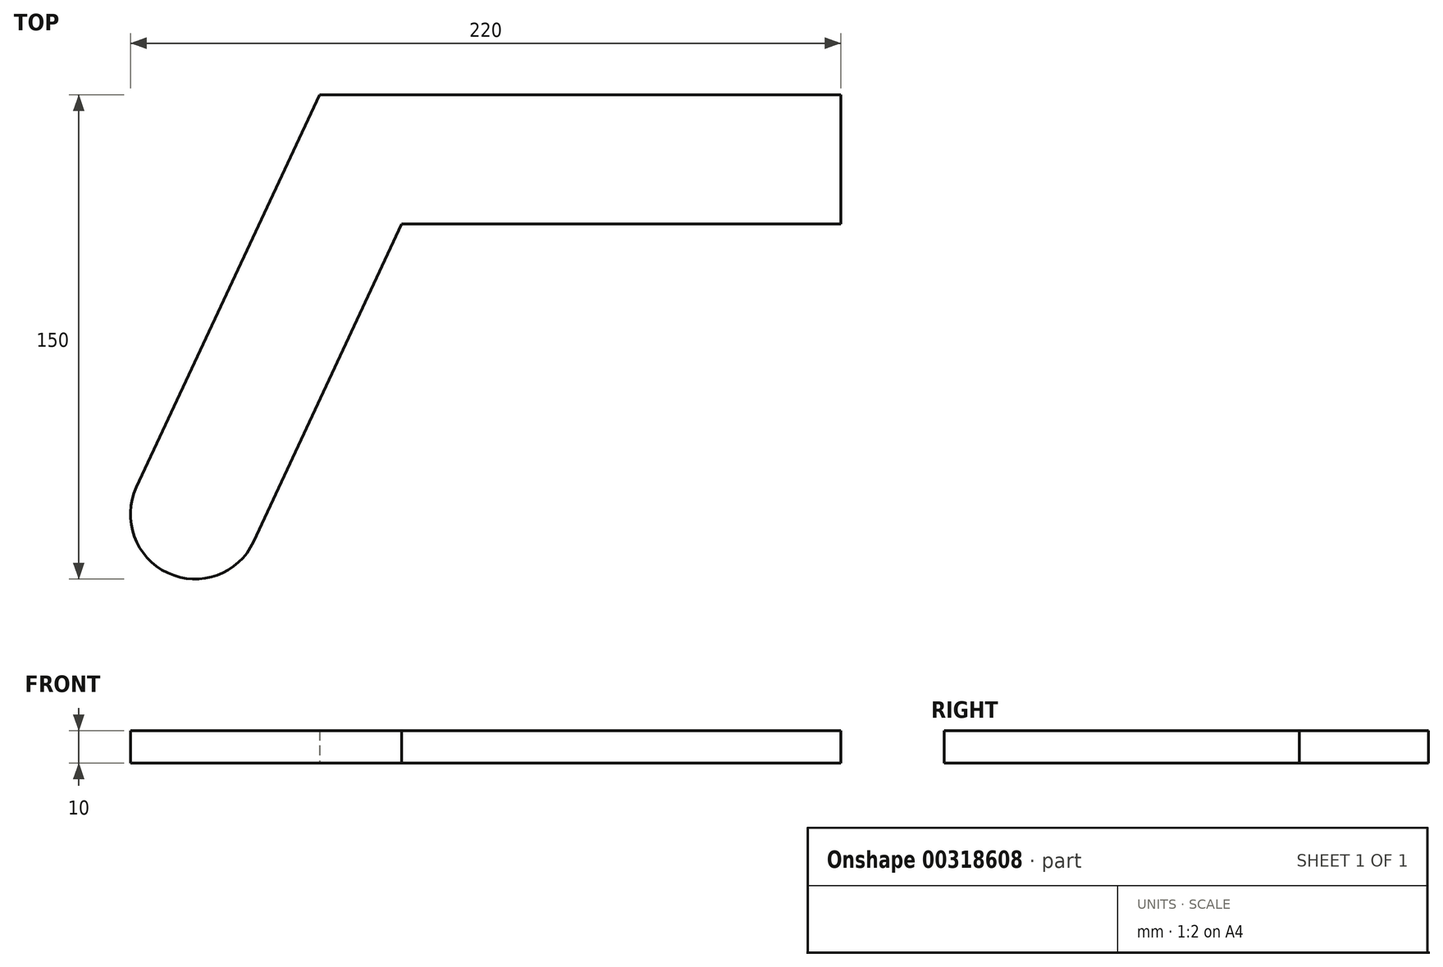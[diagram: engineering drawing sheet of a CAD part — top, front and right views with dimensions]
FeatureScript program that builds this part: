
annotation { "Feature Type Name" : "Feature", "Feature Type Description" : "" }
export const myFeature = defineFeature(function(context is Context, id is Id, definition is map)
    precondition{}
    {
        {
            var Q0;
            Q0=qCreatedBy(makeId("Top.planeOp"),FACE);
            var sketch = newSketch(context, id + "F0", { "sketchPlane" : qUnion([Q0])});
            skLineSegment(sketch, "E0", {"start": v(-18.13, 8.45) * mm, "end": v(38.55, 130) * mm});
            skLineSegment(sketch, "E1", {"start": v(38.55, 130) * mm, "end": v(200, 130) * mm});
            skLineSegment(sketch, "E2", {"start": v(200, 130) * mm, "end": v(200, 90) * mm});
            skLineSegment(sketch, "E3", {"start": v(200, 90) * mm, "end": v(64.04, 90) * mm});
            skLineSegment(sketch, "E4", {"start": v(64.04, 90) * mm, "end": v(18.13, -8.45) * mm});
            skArc(sketch, "E5", {"start": v(-18.13, 8.45) * mm, "mid": v(-8.45, -18.13) * mm, "end": v(18.13, -8.45) * mm});
            skSolve(sketch);
        }
        {
            var Q0;
            Q0=makeQuery(id+"F0.imprint","IMPRINT",FACE,{"disambiguationData":[TD([[makeQuery(id+"F0.imprint","IMPRINT",EDGE,{"derivedFrom":sQuery(id+"F0.wireOp",EDGE,"E0")}),-1.0]])]});
            extrude(context, id + "F1", {"entities" : qUnion([Q0]), "depth" : 10 * mm});
        }
    });
